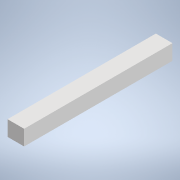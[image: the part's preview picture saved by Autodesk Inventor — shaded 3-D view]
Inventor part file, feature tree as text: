
AUTODESK INVENTOR PART (.ipt)
format: ipt  version: 2020 (Build 240168000, 168)  size: 99,840 bytes
history: native  units: in
note: dims shown in document units (in); Inventor stores cm internally (conversion verified against a paired STEP export)
features: sketch x1, plane x1, extrude x1
ambient origin geometry x8: Origin, YZ Plane, XZ Plane, XY Plane, X Axis, Y Axis, Z Axis, Center Point
bodies: Solid1 (feature_tree)
feature tree (3):
  sketch  "Sketch1"  dims[d0=1.0in d1=0.0in d3=0.5in d4=0.0344in d5=0.5in d6=0.0344in]
  plane  "Work Plane1"
  extrude  "Extrusion1"  Depth=0.5in
